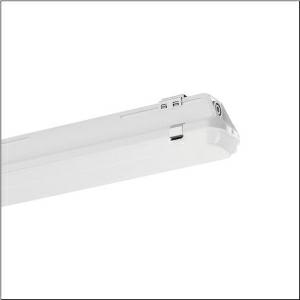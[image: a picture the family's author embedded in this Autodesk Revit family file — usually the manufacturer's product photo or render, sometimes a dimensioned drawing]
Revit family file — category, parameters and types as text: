
# Revit family: monsun_11_facade_51ff40mp360h
name_source: partatom
category: Lighting Fixtures
units: mm (PartAtom-declared; Revit-internal decimal feet)

## family parameters
Cut with Voids When Loaded = No
Host = Face
Light Source = No
Part Type = Normal
Room Calculation Point = No
Round Connector Dimension = Use Diameter
Shared = No

## types (1)
- --- (1 x LED, 5790 lm, 33.6 W, 3000K)
    Apparent Load = 34 VA
    CIE Flux Codes = 47 77 93 95 100
    Color Rendering = 80
    Color Temperature = 3000K
    Default Elevation = 1800 mm
    Description = Monsun 11 facade, damp-proof luminaire, chain hanger, primary optical cover: enclosure, of PMMA, light emission: direct distribution, primary light characteristic: symmetric, installation type: vertical mounting, horizontal mounting, surface-mounted, LED, rated luminous flux: 5.790lm, luminous efficacy: 172lm/W, light colour: 830, colour temperature: 3000K, control gear: ON/OFF Multilumen, with terminal, 3-pole, max. 2.5mm², mains connection: 220..240V, AC, 50/60Hz, rated input power: 34W, luminaire housing, of glass-fibre reinforced polyester, uncoated, bright grey, with climate membrane, for cables, Ø 8.4..12mm, incl. chain hanger, length: 1.590mm, width: 90mm, height: 88mm, clip for enclosure, of stainless steel (V2A), ceiling mounting element, of stainless steel (V2A), chain hanger, of stainless steel (V2A), protection rating (complete): IP66, insulation class (complete): insulation class I (protective earthing), certification: CE, ENEC, VDE, UKCA, protection symbol: D, impact resistance: IK06, permissible operating ambient temperature: -35..+50°C, standard: EN 60598-2-1, EN 50419, exposed outdoor area, contact your sales advisor before using the luminaires in applications with unclear chemical exposure, large temperature fluctuations or condensation-forming humidity, LABS conformity tested according to VDMA 24364:2018-05, packaging unit: 1 piece
    Height = 89 mm
    Lamp = 1 x LED
    Lamp Light Flux = 5790 lm
    Lamp Power = 33.6 W
    Lamp count = 1
    Length = 1590 mm
    Luminous efficacy = 172 lm/W
    Manufacturer = Siteco
    ModVariant = No
    Model = 51FF40MP360H
    Mounting Place = Ceiling
    Mounting Type = Surface mounted
    Number of Poles = 1
    OnlyDefault = Yes
    Power Factor = 1
    Product Name = Monsun 11 facade
    Product group = damp-proof luminaire
    ProductGroupID = 300
    Protection Class = Protection class I
    Protection Degree = IP 66
    RLX_Detail_Level = 1
    RLX_Emergency_Light_Flux = 0 lm
    RLX_Emergency_Type = 0
    RLX_Emergency_Type_DB = No
    RlxData = <blob elided: 89853 chars, md5=9b8526bc>
    Socket = socket
    Standby Power = 0 W
    System Light Flux = 5790 lm
    System Power = 34 W
    Type Comments = factory setting: luminous flux: 100 % | (A | C | E) | 77 mA
    Type Image = l_1349237.jpg
    URL = http://relux.com
    VarID = @adj_142833
    Voltage = 0 V
    Weight = 0.00 kg
    Width = 90 mm

## geometry (parser evidence)
native form markers: Blend x4, Sweep x15
no freeform markers — native parametric forms only
